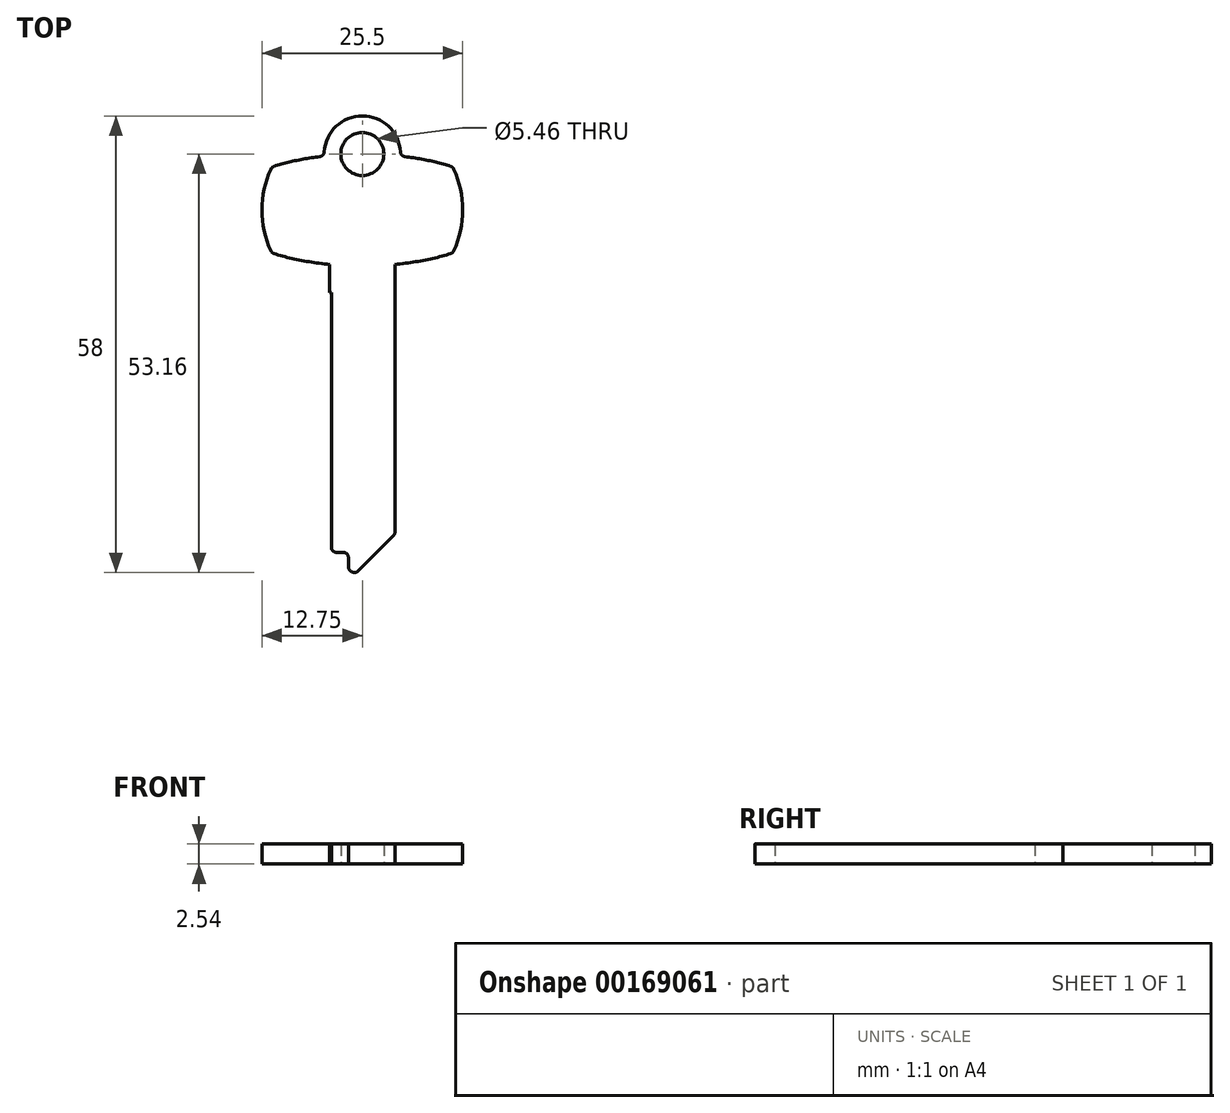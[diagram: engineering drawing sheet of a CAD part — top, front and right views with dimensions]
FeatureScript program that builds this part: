
annotation { "Feature Type Name" : "Feature", "Feature Type Description" : "" }
export const myFeature = defineFeature(function(context is Context, id is Id, definition is map)
    precondition{}
    {
        {
            var Q0;
            Q0=qCreatedBy(makeId("Top.planeOp"),FACE);
            var sketch = newSketch(context, id + "F0", { "sketchPlane" : qUnion([Q0])});
            skLineSegment(sketch, "E0", {"start": v(0, 0) * mm, "end": v(0, -14.22) * mm, "construction": true});
            skCircle(sketch, "E1", {"center": v(0, 0) * mm, "radius": 2.73 * mm});
            skArc(sketch, "E2.0", {"start": v(4.83, -0.26) * mm, "mid": v(0, 4.84) * mm, "end": v(-4.83, -0.26) * mm});
            skLineSegment(sketch, "E3", {"start": v(-12.75, -7.11) * mm, "end": v(12.75, -7.11) * mm, "construction": true});
            skPoint(sketch, "E4", {"position": v(0, -7.11) * mm});
            skEllipticalArc(sketch, "E5", {});
            skArc(sketch, "E6", {"start": v(-11.5, -1.66) * mm, "mid": v(-12.75, -7.11) * mm, "end": v(-11.5, -12.57) * mm});
            skLineSegment(sketch, "E7", {"start": v(-11.5, -1.66) * mm, "end": v(-11.5, -12.57) * mm, "construction": true});
            skArc(sketch, "E8.MirrorCS", {"start": v(11.5, -1.66) * mm, "mid": v(12.75, -7.11) * mm, "end": v(11.5, -12.57) * mm});
            skEllipticalArc(sketch, "E9.trimOffspring", {});
            skLineSegment(sketch, "E10", {"start": v(0.05, -53.7) * mm, "end": v(0.05, 5.12) * mm, "construction": true});
            skPoint(sketch, "E10.endSnap0", {"position": v(0.05, 5.12) * mm});
            skPoint(sketch, "E11.orphan", {"position": v(0.05, 6.82) * mm});
            const initialGuessF0  = {"E5": [0, -0.007112, 1, 0, 0.017907, 0.007112, 4.015594456892737, 5.409183503876642], "E9.trimOffspring": [0, -0.007112, 1, 0, 0.017907, 0.007112, 0.8740018033029436, 2.2675908502868496]};
            skSetInitialGuess(sketch, initialGuessF0);
            skSolve(sketch);
        }
        {
            var Q0;
            Q0=makeQuery(id+"F0.imprint","IMPRINT",FACE,{"disambiguationData":[TD([[makeQuery(id+"F0.imprint","IMPRINT",EDGE,{"derivedFrom":sQuery(id+"F0.wireOp",EDGE,"E5")}),1.0]])]});
            var Q1;
            {var subQ4=sQuery(id+"F0.wireOp",EDGE,"E2.0");Q1=makeQuery(id+"F0.imprint","IMPRINT",FACE,{"disambiguationData":[TD([[makeQuery(id+"F0.imprint","IMPRINT",EDGE,{"derivedFrom":subQ4}),1.0]])]});}
            extrude(context, id + "F1", {"entities" : qUnion([Q0, Q1]), "depth" : 2.54 * mm});
        }
        {
            var Q0;
            Q0=qCreatedBy(makeId("Top.planeOp"),FACE);
            var sketch = newSketch(context, id + "F2", { "sketchPlane" : qUnion([Q0])});
            skLineSegment(sketch, "E12", {"start": v(0, -14.22) * mm, "end": v(0, -52.46) * mm, "construction": true});
            skLineSegment(sketch, "E13", {"start": v(-4.14, -14.03) * mm, "end": v(-4.14, -17.59) * mm});
            skLineSegment(sketch, "E14", {"start": v(-4.14, -17.59) * mm, "end": v(-3.94, -17.59) * mm});
            skLineSegment(sketch, "E15", {"start": v(-3.94, -17.59) * mm, "end": v(-3.94, -50.6) * mm});
            skLineSegment(sketch, "E16", {"start": v(-3.94, -50.6) * mm, "end": v(-1.78, -50.6) * mm});
            skLineSegment(sketch, "E17", {"start": v(-1.78, -50.6) * mm, "end": v(-1.78, -52.4) * mm});
            skLineSegment(sketch, "E18", {"start": v(-0.48, -52.94) * mm, "end": v(3.92, -48.54) * mm});
            skLineSegment(sketch, "E19", {"start": v(4.14, -48) * mm, "end": v(4.14, -14.03) * mm});
            skEllipticalArc(sketch, "E20.0", {});
            skPoint(sketch, "E21.orphan", {"position": v(-11.5, -12.57) * mm});
            skPoint(sketch, "E22.orphan", {"position": v(11.5, -12.57) * mm});
            skPoint(sketch, "E23.visualSharp", {"position": v(-1.78, -54.24) * mm});
            skArc(sketch, "E23.filletArc", {"start": v(-1.78, -52.4) * mm, "mid": v(-1.3, -53.1) * mm, "end": v(-0.48, -52.94) * mm});
            skPoint(sketch, "E24.visualSharp", {"position": v(4.14, -48.32) * mm});
            skArc(sketch, "E24.filletArc", {"start": v(3.92, -48.54) * mm, "mid": v(4.08, -48.3) * mm, "end": v(4.14, -48) * mm});
            const initialGuessF2  = {"E20.0": [0, -0.007112, 1, 0, 0.017907, 0.007112, 4.4790722282272615, 4.945705732542118]};
            skSetInitialGuess(sketch, initialGuessF2);
            skSolve(sketch);
        }
        {
            var Q0;
            Q0 = qSketchRegion(id + "F2", true);
            var Q1;
            Q1=makeQuery(id+"F1.opExtrude","CAP_FACE",FACE,{"disambiguationData":[OSD([sQuery(id+"F0.wireOp",EDGE,"E1"),sQuery(id+"F0.wireOp",EDGE,"E2.0"),sQuery(id+"F0.wireOp",EDGE,"E5"),sQuery(id+"F0.wireOp",EDGE,"E6"),sQuery(id+"F0.wireOp",EDGE,"E8.MirrorCS"),sQuery(id+"F0.wireOp",EDGE,"E9.trimOffspring")])],"isStart":false});
            extrude(context, id + "F3", {"entities" : qUnion([Q0]), "operationType" : NewBodyOperationType.ADD, "endBound" : BoundingType.UP_TO_SURFACE, "endBoundEntityFace" : qUnion([Q1]), "depth" : 25.4 * mm});
        }
        {
            var Q0;
            Q0=makeQuery(id+"F3.opExtrude","SWEPT_EDGE",EDGE,{"disambiguationData":[OSD([sQuery(id+"F2.wireOp",EDGE,"E13"),sQuery(id+"F2.wireOp",EDGE,"E20.0")])]});
            var Q1;
            Q1=makeQuery(id+"F3.opExtrude","SWEPT_EDGE",EDGE,{"disambiguationData":[OSD([sQuery(id+"F2.wireOp",EDGE,"E19"),sQuery(id+"F2.wireOp",EDGE,"E20.0")])]});
            var Q2;
            Q2=makeQuery(id+"F1.opExtrude","SWEPT_EDGE",EDGE,{"disambiguationData":[OSD([sQuery(id+"F0.wireOp",EDGE,"E5"),sQuery(id+"F0.wireOp",EDGE,"E8.MirrorCS")])]});
            var Q3;
            Q3=makeQuery(id+"F1.opExtrude","SWEPT_EDGE",EDGE,{"disambiguationData":[OSD([sQuery(id+"F0.wireOp",EDGE,"E8.MirrorCS"),sQuery(id+"F0.wireOp",EDGE,"E9.trimOffspring")])]});
            var Q4;
            Q4=makeQuery(id+"F1.opExtrude","SWEPT_EDGE",EDGE,{"disambiguationData":[OSD([sQuery(id+"F0.wireOp",EDGE,"E6"),sQuery(id+"F0.wireOp",EDGE,"E9.trimOffspring")])]});
            var Q5;
            Q5=makeQuery(id+"F1.opExtrude","SWEPT_EDGE",EDGE,{"disambiguationData":[OSD([sQuery(id+"F0.wireOp",EDGE,"E5"),sQuery(id+"F0.wireOp",EDGE,"E6")])]});
            var Q6;
            Q6=makeQuery(id+"F3.opExtrude","SWEPT_EDGE",EDGE,{"disambiguationData":[OSD([sQuery(id+"F2.wireOp",EDGE,"E15"),sQuery(id+"F2.wireOp",EDGE,"E16")])]});
            var Q7;
            Q7=makeQuery(id+"F3.opExtrude","SWEPT_EDGE",EDGE,{"disambiguationData":[OSD([sQuery(id+"F2.wireOp",EDGE,"E16"),sQuery(id+"F2.wireOp",EDGE,"E17")])]});
            var Q8;
            {var subQ0=sQuery(id+"F0.wireOp",EDGE,"E9.trimOffspring");var subQ1=sQuery(id+"F0.wireOp",EDGE,"E2.0");Q8=makeQuery(id+"F1.opExtrude","SWEPT_EDGE",EDGE,{"disambiguationData":[OSD([subQ1,subQ0]),TDD([makeQuery(id+"F0.imprint","INTERSECT",VERTEX,{"disambiguationData":[OD(1.0)],"derivedFrom":[subQ1,subQ0]})])]});}
            var Q9;
            {var subQ0=sQuery(id+"F0.wireOp",EDGE,"E9.trimOffspring");var subQ1=sQuery(id+"F0.wireOp",EDGE,"E2.0");Q9=makeQuery(id+"F1.opExtrude","SWEPT_EDGE",EDGE,{"disambiguationData":[OSD([subQ1,subQ0]),TDD([makeQuery(id+"F0.imprint","INTERSECT",VERTEX,{"disambiguationData":[OD(0.0)],"derivedFrom":[subQ1,subQ0]})])]});}
            fillet(context, id + "F4", {"entities" : qUnion([Q0, Q1, Q2, Q3, Q4, Q5, Q6, Q7, Q8, Q9]), "radius" : 0.64 * mm, "tangentPropagation" : true, "allowEdgeOverflow" : false});
        }
    });
